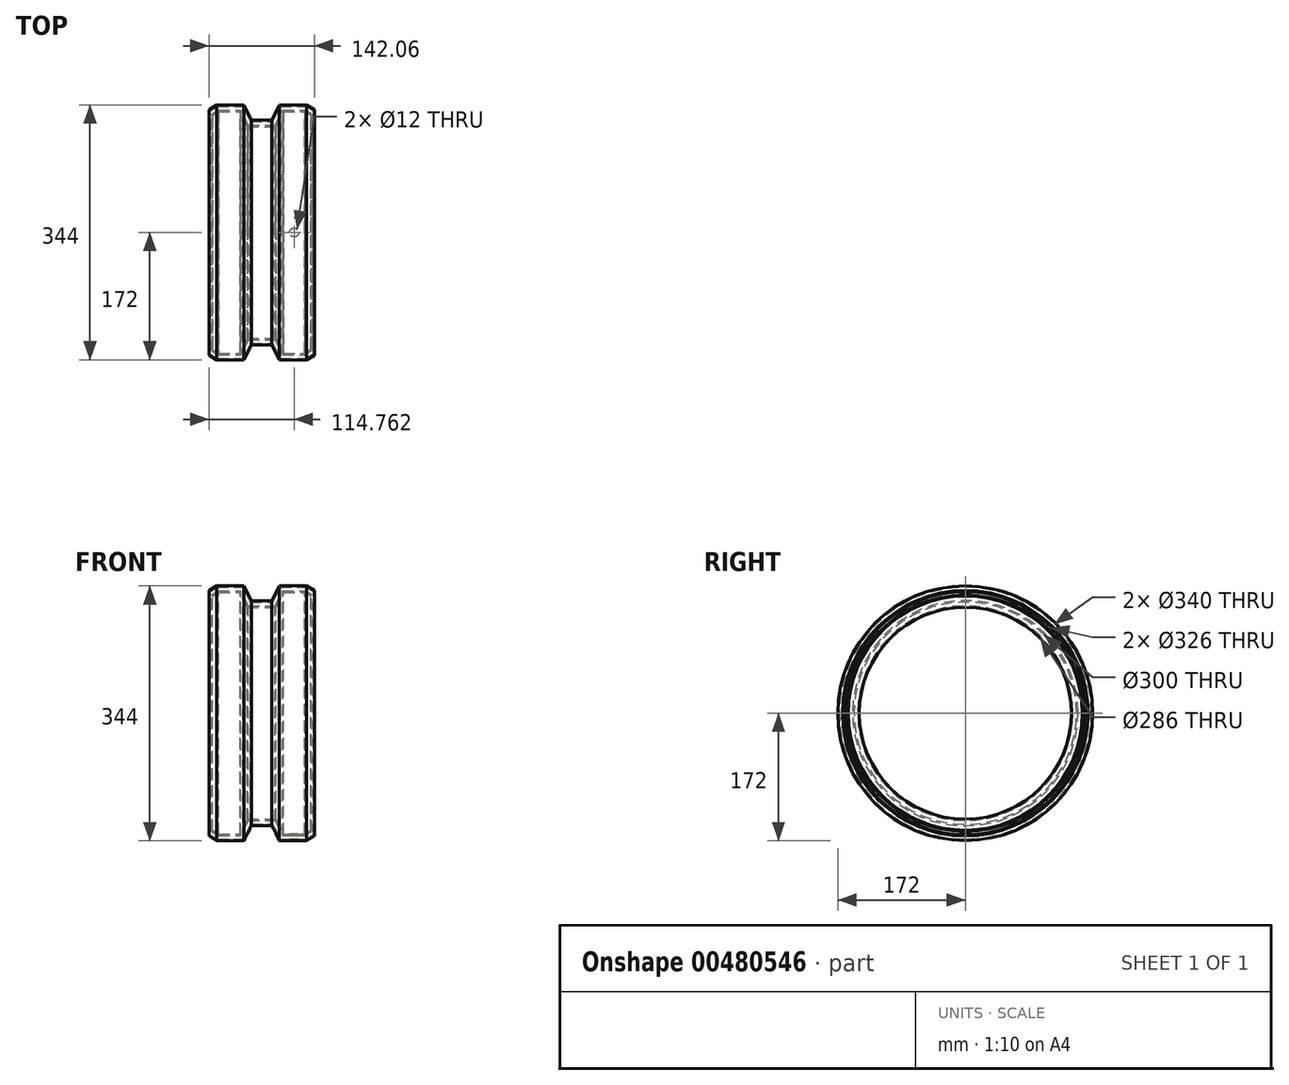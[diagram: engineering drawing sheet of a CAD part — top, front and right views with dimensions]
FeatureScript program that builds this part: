
annotation { "Feature Type Name" : "Feature", "Feature Type Description" : "" }
export const myFeature = defineFeature(function(context is Context, id is Id, definition is map)
    precondition{}
    {
        {
            var Q0;
            Q0=qCreatedBy(makeId("Front.planeOp"),FACE);
            var sketch = newSketch(context, id + "F0", { "sketchPlane" : qUnion([Q0])});
            skLineSegment(sketch, "E0", {"start": v(0, 0) * mm, "end": v(0, -150) * mm});
            skLineSegment(sketch, "E1", {"start": v(0, -150) * mm, "end": v(-15, -150) * mm});
            skLineSegment(sketch, "E2", {"start": v(-15, -150) * mm, "end": v(-25, -170) * mm});
            skLineSegment(sketch, "E3", {"start": v(-25, -170) * mm, "end": v(-60, -170) * mm});
            skLineSegment(sketch, "E4", {"start": v(-60, -170) * mm, "end": v(-70, -164) * mm});
            skLineSegment(sketch, "E5.MirrorCS", {"start": v(0, -150) * mm, "end": v(15, -150) * mm});
            skLineSegment(sketch, "E6.MirrorCS", {"start": v(15, -150) * mm, "end": v(25, -170) * mm});
            skLineSegment(sketch, "E7.MirrorCS", {"start": v(60, -170) * mm, "end": v(70, -164) * mm});
            skLineSegment(sketch, "E8.MirrorCS", {"start": v(25, -170) * mm, "end": v(60, -170) * mm});
            skLineSegment(sketch, "E9", {"start": v(0, 0) * mm, "end": v(-140.48, 0) * mm});
            skLineSegment(sketch, "E10.0", {"start": v(-58.62, -165) * mm, "end": v(-67.43, -159.71) * mm});
            skLineSegment(sketch, "E10.1", {"start": v(-28.1, -165) * mm, "end": v(-58.62, -165) * mm});
            skLineSegment(sketch, "E10.2", {"start": v(-18.1, -145) * mm, "end": v(-28.1, -165) * mm});
            skLineSegment(sketch, "E10.3", {"start": v(0, -145) * mm, "end": v(-18.1, -145) * mm});
            skLineSegment(sketch, "E10.4", {"start": v(58.62, -165) * mm, "end": v(67.43, -159.71) * mm});
            skLineSegment(sketch, "E10.5", {"start": v(28.1, -165) * mm, "end": v(58.62, -165) * mm});
            skLineSegment(sketch, "E10.6", {"start": v(18.1, -145) * mm, "end": v(28.1, -165) * mm});
            skLineSegment(sketch, "E10.7", {"start": v(0, -145) * mm, "end": v(18.1, -145) * mm});
            skLineSegment(sketch, "E11.0", {"start": v(-58.06, -163) * mm, "end": v(-66.4, -158) * mm});
            skLineSegment(sketch, "E11.1", {"start": v(-29.33, -163) * mm, "end": v(-58.06, -163) * mm});
            skLineSegment(sketch, "E11.2", {"start": v(-19.33, -143) * mm, "end": v(-29.33, -163) * mm});
            skLineSegment(sketch, "E11.3", {"start": v(0, -143) * mm, "end": v(-19.33, -143) * mm});
            skLineSegment(sketch, "E11.4", {"start": v(58.06, -163) * mm, "end": v(66.4, -158) * mm});
            skLineSegment(sketch, "E11.5", {"start": v(29.33, -163) * mm, "end": v(58.06, -163) * mm});
            skLineSegment(sketch, "E11.6", {"start": v(19.33, -143) * mm, "end": v(29.33, -163) * mm});
            skLineSegment(sketch, "E11.7", {"start": v(0, -143) * mm, "end": v(19.33, -143) * mm});
            skLineSegment(sketch, "E12", {"start": v(-67.43, -159.71) * mm, "end": v(-66.4, -158) * mm});
            skLineSegment(sketch, "E13", {"start": v(67.43, -159.71) * mm, "end": v(66.4, -158) * mm});
            skLineSegment(sketch, "E14.0", {"start": v(60.55, -172) * mm, "end": v(71.03, -165.71) * mm});
            skLineSegment(sketch, "E14.1", {"start": v(23.76, -172) * mm, "end": v(60.55, -172) * mm});
            skLineSegment(sketch, "E14.2", {"start": v(13.76, -152) * mm, "end": v(23.76, -172) * mm});
            skLineSegment(sketch, "E14.3", {"start": v(0, -152) * mm, "end": v(13.76, -152) * mm});
            skLineSegment(sketch, "E14.4", {"start": v(-60.55, -172) * mm, "end": v(-71.03, -165.71) * mm});
            skLineSegment(sketch, "E14.5", {"start": v(-23.76, -172) * mm, "end": v(-60.55, -172) * mm});
            skLineSegment(sketch, "E14.6", {"start": v(-13.76, -152) * mm, "end": v(-23.76, -172) * mm});
            skLineSegment(sketch, "E14.7", {"start": v(0, -152) * mm, "end": v(-13.76, -152) * mm});
            skLineSegment(sketch, "E15", {"start": v(70, -164) * mm, "end": v(71.03, -165.71) * mm});
            skLineSegment(sketch, "E16", {"start": v(-70, -164) * mm, "end": v(-71.03, -165.71) * mm});
            skSolve(sketch);
        }
        {
            var Q0;
            Q0=makeQuery(id+"F0.imprint","IMPRINT",FACE,{"disambiguationData":[TD([[makeQuery(id+"F0.imprint","IMPRINT",EDGE,{"derivedFrom":sQuery(id+"F0.wireOp",EDGE,"E10.4")}),1.0]])]});
            var Q1;
            Q1=makeQuery(id+"F0.imprint","IMPRINT",FACE,{"disambiguationData":[TD([[makeQuery(id+"F0.imprint","IMPRINT",EDGE,{"derivedFrom":sQuery(id+"F0.wireOp",EDGE,"E1")}),1.0]])]});
            var Q2;
            Q2=makeQuery(id+"F0.imprint","IMPRINT",FACE,{"disambiguationData":[TD([[makeQuery(id+"F0.imprint","IMPRINT",EDGE,{"derivedFrom":sQuery(id+"F0.wireOp",EDGE,"E10.0")}),-1.0]])]});
            var Q3;
            Q3=sQuery(id+"F0.wireOp",EDGE,"E9");
            revolve(context, id + "F1", {"entities" : qUnion([Q0, Q1, Q2]), "axis" : qUnion([Q3]), "revolveType" : RevolveType.FULL});
        }
        {
            var Q0;
            Q0 = qSketchRegion(id + "F0", true);
            var Q1;
            Q1=sQuery(id+"F0.wireOp",EDGE,"E11.5");
            extrude(context, id + "F2", {"entities" : qUnion([Q0]), "bodyType" : ToolBodyType.SURFACE, "surfaceEntities" : qUnion([Q1]), "endBound" : BoundingType.SYMMETRIC, "depth" : 190.2 * mm});
        }
        {
            var Q0;
            Q0=makeQuery(id+"F2.opExtrude","SWEPT_BODY",BODY,{"disambiguationData":[OSD([sQuery(id+"F0.wireOp",EDGE,"E11.5")])]});
            transform(context, id + "F3", {"entities" : qUnion([Q0]), "transformType" : TransformType.TRANSLATION_3D, "dx" : 0 * mm, "dy" : 0 * mm, "dz" : 5 * mm, "makeCopy" : false});
        }
        {
            var Q0;
            Q0=makeQuery(id+"F2.opExtrude","SWEPT_FACE",FACE,{"disambiguationData":[OSD([sQuery(id+"F0.wireOp",EDGE,"E11.5")])]});
            var sketch = newSketch(context, id + "F4", { "sketchPlane" : qUnion([Q0])});
            skPoint(sketch, "E17", {"position": v(43.73, 0) * mm});
            skSolve(sketch);
        }
        {
            var Q0;
            Q0=sQuery(id+"F4.wireOp",VERTEX,"E17");
            var Q1;
            Q1=makeQuery(id+"F1.opRevolve","SWEPT_BODY",BODY,{"disambiguationData":[OSD([sQuery(id+"F0.wireOp",EDGE,"E10.0"),sQuery(id+"F0.wireOp",EDGE,"E10.1"),sQuery(id+"F0.wireOp",EDGE,"E10.2"),sQuery(id+"F0.wireOp",EDGE,"E10.3"),sQuery(id+"F0.wireOp",EDGE,"E10.4"),sQuery(id+"F0.wireOp",EDGE,"E10.5"),sQuery(id+"F0.wireOp",EDGE,"E10.6"),sQuery(id+"F0.wireOp",EDGE,"E10.7"),sQuery(id+"F0.wireOp",EDGE,"E11.0"),sQuery(id+"F0.wireOp",EDGE,"E11.1"),sQuery(id+"F0.wireOp",EDGE,"E11.2"),sQuery(id+"F0.wireOp",EDGE,"E11.3"),sQuery(id+"F0.wireOp",EDGE,"E11.4"),sQuery(id+"F0.wireOp",EDGE,"E11.5"),sQuery(id+"F0.wireOp",EDGE,"E11.6"),sQuery(id+"F0.wireOp",EDGE,"E11.7"),sQuery(id+"F0.wireOp",EDGE,"E12"),sQuery(id+"F0.wireOp",EDGE,"E13")])]});
            var Q2;
            Q2=makeQuery(id+"F1.opRevolve","SWEPT_BODY",BODY,{"disambiguationData":[OSD([sQuery(id+"F0.wireOp",EDGE,"E1"),sQuery(id+"F0.wireOp",EDGE,"E2"),sQuery(id+"F0.wireOp",EDGE,"E3"),sQuery(id+"F0.wireOp",EDGE,"E4"),sQuery(id+"F0.wireOp",EDGE,"E5.MirrorCS"),sQuery(id+"F0.wireOp",EDGE,"E6.MirrorCS"),sQuery(id+"F0.wireOp",EDGE,"E7.MirrorCS"),sQuery(id+"F0.wireOp",EDGE,"E8.MirrorCS"),sQuery(id+"F0.wireOp",EDGE,"E14.0"),sQuery(id+"F0.wireOp",EDGE,"E14.1"),sQuery(id+"F0.wireOp",EDGE,"E14.2"),sQuery(id+"F0.wireOp",EDGE,"E14.3"),sQuery(id+"F0.wireOp",EDGE,"E14.4"),sQuery(id+"F0.wireOp",EDGE,"E14.5"),sQuery(id+"F0.wireOp",EDGE,"E14.6"),sQuery(id+"F0.wireOp",EDGE,"E14.7"),sQuery(id+"F0.wireOp",EDGE,"E15"),sQuery(id+"F0.wireOp",EDGE,"E16")])]});
            hole(context, id + "F5", {"style" : HoleStyle.SIMPLE, "endStyle" : HoleEndStyle.THROUGH, "oppositeDirection" : true, "standardTappedOrClearance" : lookupTablePath({ "standard" : "ISO", "size" : "12", "type" : "Drilled" }), "standardBlindInLast" : lookupTablePath({ "standard" : "ISO", "size" : "12", "type" : "Drilled" }), "holeDiameter" : 12 * mm, "isTappedThrough" : true, "tappedDepth" : 12 * mm, "tapClearance" : 3, "locations" : qUnion([Q0]), "scope" : qUnion([Q1, Q2])});
        }
    });
